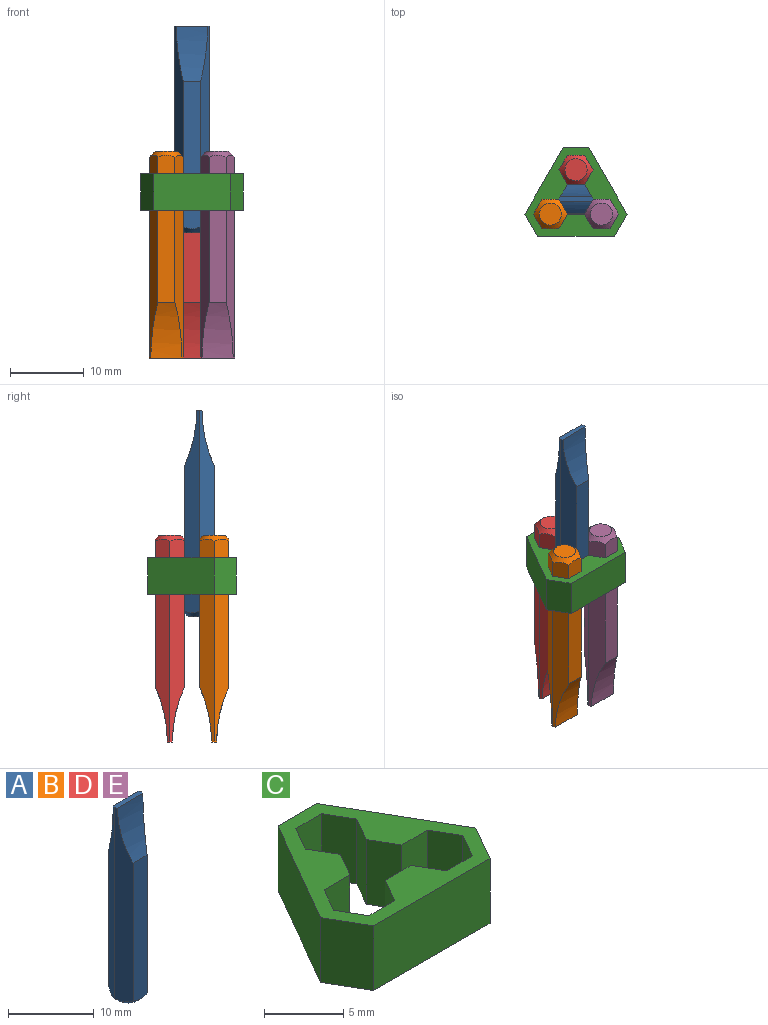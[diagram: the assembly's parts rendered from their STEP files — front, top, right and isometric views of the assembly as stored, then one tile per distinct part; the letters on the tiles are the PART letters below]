
ASSEMBLY  parts=5 mates=6
PART A: 11 faces, bbox 4.6x4.6x28 mm
  f0: plane 20x2.31mm, normal (0,1,0), area 45.9mm2, adj f2,f6,f7,f9
  f1: plane 4.62x0.7mm, normal (0,0,1), area 3.1mm2, adj f2,f3,f5,f6,f7,f8
  f2: plane 27.5x2mm, normal (-0.87,0.5,0), area 53.6mm2, adj f0,f1,f3,f7,f9
  f3: plane 27.5x2mm, normal (-0.87,-0.5,0), area 53.6mm2, adj f1,f2,f4,f8,f9
  f4: plane 20x2.31mm, normal (0,-1,0), area 45.9mm2, adj f3,f5,f8,f9
  f5: plane 27.5x2mm, normal (0.87,-0.5,0), area 53.6mm2, adj f1,f4,f6,f8,f9
  f6: plane 27.5x2mm, normal (0.87,0.5,0), area 53.6mm2, adj f0,f1,f5,f7,f9
  f7: cylinder r=17.87mm len=7.5mm, axis (1,0,0), area 27.7mm2, adj f0,f1,f2,f6
  f8: cylinder r=17.87mm len=7.5mm, axis (1,0,0), area 27.7mm2, adj f1,f3,f4,f5
  f9: cone r=1.5mm half-angle=45deg, axis (0,0,1), area 9.6mm2, adj f0,f2,f3,f4,f5,f6,f10
  f10: plane 3x3mm, normal (0,0,-1), area 7.1mm2, adj f9
PART B: same geometry as A
PART C: 26 faces, bbox 13.9x12x5 mm
  f0: plane 5x2mm, normal (-0.87,-0.5,0), area 11.5mm2, adj f1,f23,f24,f25
  f1: plane 5x2.31mm, normal (0,-1,0), area 11.5mm2, adj f0,f2,f24,f25
  f2: plane 5x2mm, normal (-0.87,-0.5,0), area 11.5mm2, adj f1,f3,f24,f25
  f3: plane 5x2mm, normal (-0.87,0.5,0), area 11.5mm2, adj f2,f4,f24,f25
  f4: plane 5x2.31mm, normal (0,1,0), area 11.5mm2, adj f3,f5,f24,f25
  f5: plane 5x2mm, normal (0.87,0.5,0), area 11.5mm2, adj f4,f6,f24,f25
  f6: plane 5x2.31mm, normal (0,1,0), area 11.5mm2, adj f5,f7,f24,f25
  f7: plane 5x2mm, normal (-0.87,0.5,0), area 11.5mm2, adj f6,f8,f24,f25
  f8: plane 5x2.31mm, normal (0,1,0), area 11.5mm2, adj f7,f9,f24,f25
  f9: plane 5x2mm, normal (0.87,0.5,0), area 11.5mm2, adj f8,f10,f24,f25
  f10: plane 5x2mm, normal (0.87,-0.5,0), area 11.5mm2, adj f9,f11,f24,f25
  f11: plane 5x2.31mm, normal (0,-1,0), area 11.5mm2, adj f10,f12,f24,f25
  f12: plane 5x2mm, normal (0.87,-0.5,0), area 11.5mm2, adj f11,f13,f24,f25
  f13: plane 5x2mm, normal (0.87,0.5,0), area 11.5mm2, adj f12,f14,f24,f25
  f14: plane 5x2mm, normal (0.87,-0.5,0), area 11.5mm2, adj f13,f15,f24,f25
  f15: plane 5x2.31mm, normal (0,-1,0), area 11.5mm2, adj f14,f16,f24,f25
  f16: plane 5x2mm, normal (-0.87,-0.5,0), area 11.5mm2, adj f15,f23,f24,f25
  f17: plane 10.39x5mm, normal (0,-1,0), area 52mm2, adj f18,f22,f24,f25
  f18: plane 5x3mm, normal (0.87,-0.5,0), area 17.3mm2, adj f17,f19,f24,f25
  f19: plane 9x5.2mm, normal (0.87,0.5,0), area 52mm2, adj f18,f20,f24,f25
  f20: plane 5x3.46mm, normal (0,1,0), area 17.3mm2, adj f19,f21,f24,f25
  f21: plane 9x5.2mm, normal (-0.87,0.5,0), area 52mm2, adj f20,f22,f24,f25
  f22: plane 5x3mm, normal (-0.87,-0.5,0), area 17.3mm2, adj f17,f21,f24,f25
  f23: plane 5x2mm, normal (-0.87,0.5,0), area 11.5mm2, adj f0,f16,f24,f25
  f24: plane 13.86x12mm, normal (0,0,1), area 58.9mm2, adj f0,f1,f2,f3,f4,f5,f6,f7
  f25: plane 13.86x12mm, normal (0,0,-1), area 58.9mm2, adj f0,f1,f2,f3,f4,f5,f6,f7
PART D: same geometry as A
PART E: same geometry as A
PLACE A rot(axis=(0,0,1),180deg) t=(0,0,-78.32)mm
PLACE B rot(axis=(0,-1,0),180deg) t=(-3.46,-2,-67.32)mm
PLACE C t=(0,0,-75.32)mm
PLACE D rot(axis=(0,1,0),180deg) t=(0,4,-67.32)mm
PLACE E rot(axis=(0,-1,0),180deg) t=(3.46,-2,-67.32)mm
MATE slider C.f24 <-> A.f1  axis (0,0,1) through (2.31,0,-70.32)mm
MATE slider E.f1 <-> C.f25  axis (0,0,-1) through (5.77,-2,-95.32)mm
MATE planar B.f9 <-> D.f9  axis (0,0,1) through (-3.46,-2,-67.32)mm
MATE slider B.f1 <-> C.f25  axis (0,0,-1) through (-5.77,-2,-95.32)mm
MATE slider D.f1 <-> C.f25  axis (0,0,-1) through (-2.31,4,-95.32)mm
MATE planar E.f9 <-> D.f9  axis (0,0,1) through (3.46,-2,-67.32)mm
